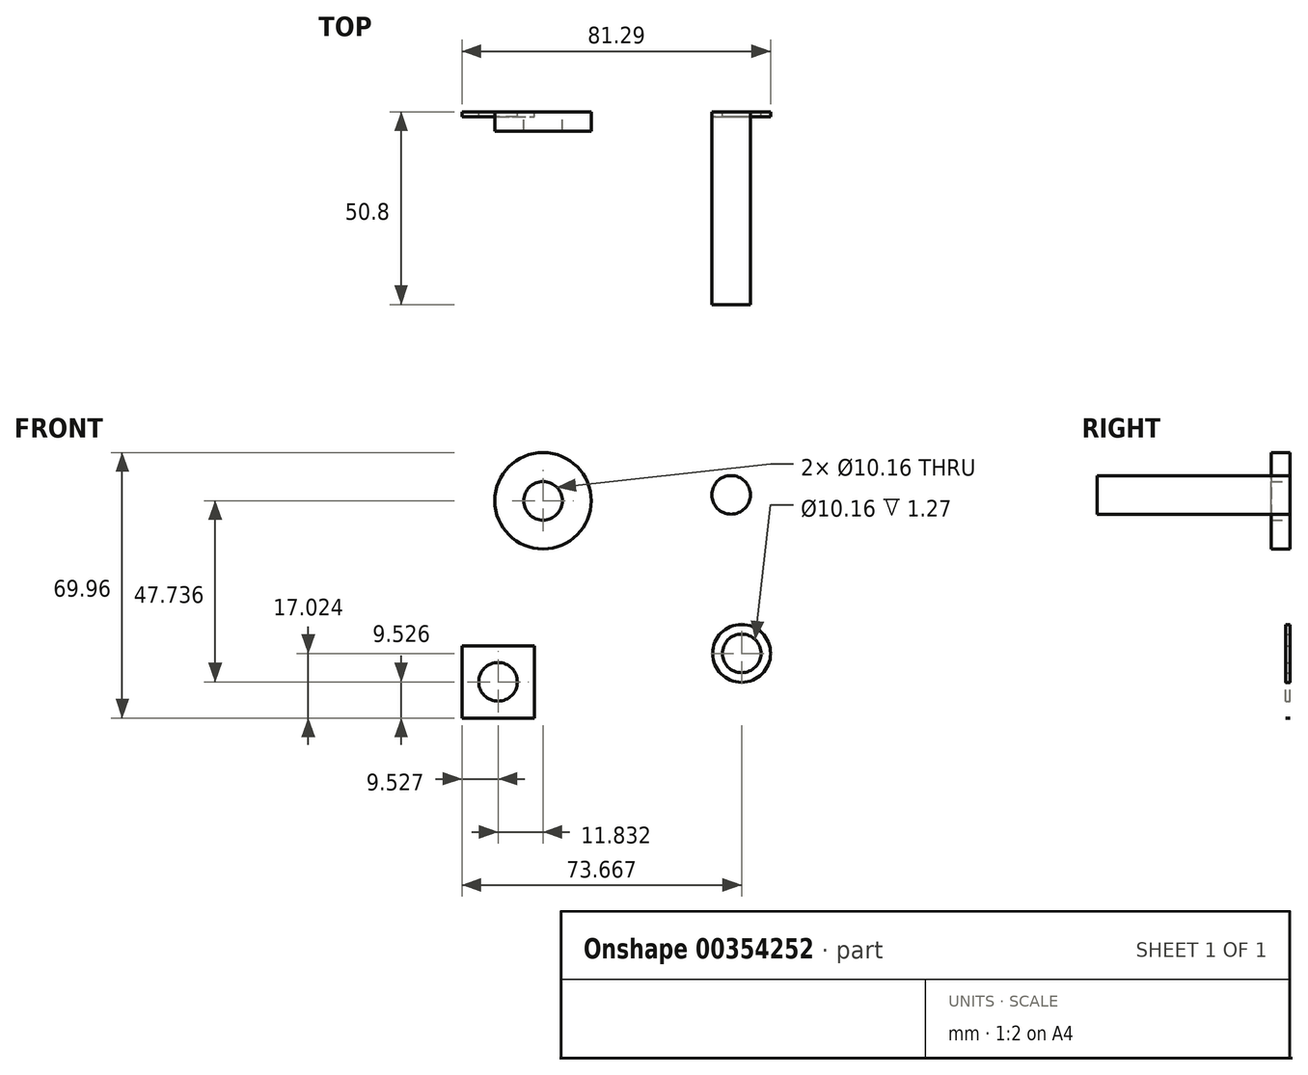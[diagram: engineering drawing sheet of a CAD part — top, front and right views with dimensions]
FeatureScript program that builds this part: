
annotation { "Feature Type Name" : "Feature", "Feature Type Description" : "" }
export const myFeature = defineFeature(function(context is Context, id is Id, definition is map)
    precondition{}
    {
        {
            var Q0;
            Q0=qCreatedBy(makeId("Front.planeOp"),FACE);
            var sketch = newSketch(context, id + "F0", { "sketchPlane" : qUnion([Q0])});
            skCircle(sketch, "E0", {"center": v(-24.76, 21.51) * mm, "radius": 12.7 * mm});
            skCircle(sketch, "E1", {"center": v(-24.76, 21.51) * mm, "radius": 5.08 * mm});
            skSolve(sketch);
        }
        {
            var Q0;
            Q0=makeQuery(id+"F0.imprint","IMPRINT",FACE,{"disambiguationData":[TD([[makeQuery(id+"F0.imprint","IMPRINT",EDGE,{"derivedFrom":sQuery(id+"F0.wireOp",EDGE,"E0")}),1.0]])]});
            extrude(context, id + "F1", {"entities" : qUnion([Q0]), "depth" : 5.08 * mm});
        }
        {
            var Q0;
            Q0=qCreatedBy(makeId("Front.planeOp"),FACE);
            var sketch = newSketch(context, id + "F2", { "sketchPlane" : qUnion([Q0])});
            skCircle(sketch, "E2", {"center": v(24.76, 23.06) * mm, "radius": 5.08 * mm});
            skSolve(sketch);
        }
        {
            var Q0;
            Q0=makeQuery(id+"F2.imprint","IMPRINT",FACE,{"disambiguationData":[TD([[makeQuery(id+"F2.imprint","IMPRINT",EDGE,{"derivedFrom":sQuery(id+"F2.wireOp",EDGE,"E2")}),1.0]])]});
            extrude(context, id + "F3", {"entities" : qUnion([Q0]), "depth" : 50.8 * mm});
        }
        {
            var Q0;
            Q0=qCreatedBy(makeId("Front.planeOp"),FACE);
            var sketch = newSketch(context, id + "F4", { "sketchPlane" : qUnion([Q0])});
            skCircle(sketch, "E3", {"center": v(-36.6, -26.22) * mm, "radius": 5.08 * mm});
            skLineSegment(sketch, "E4.bottom", {"start": v(-46.12, -16.7) * mm, "end": v(-27.07, -16.7) * mm});
            skLineSegment(sketch, "E4.top", {"start": v(-46.12, -35.75) * mm, "end": v(-27.07, -35.75) * mm});
            skLineSegment(sketch, "E4.left", {"start": v(-46.12, -16.7) * mm, "end": v(-46.12, -35.75) * mm});
            skLineSegment(sketch, "E4.right", {"start": v(-27.07, -16.7) * mm, "end": v(-27.07, -35.75) * mm});
            skSolve(sketch);
        }
        {
            var Q0;
            Q0=makeQuery(id+"F4.imprint","IMPRINT",FACE,{"disambiguationData":[TD([[makeQuery(id+"F4.imprint","IMPRINT",EDGE,{"derivedFrom":sQuery(id+"F4.wireOp",EDGE,"E3")}),-1.0]])]});
            extrude(context, id + "F5", {"entities" : qUnion([Q0]), "depth" : 1.27 * mm});
        }
        {
            var Q0;
            Q0=qCreatedBy(makeId("Front.planeOp"),FACE);
            var sketch = newSketch(context, id + "F6", { "sketchPlane" : qUnion([Q0])});
            skCircle(sketch, "E5", {"center": v(27.55, -18.73) * mm, "radius": 5.08 * mm});
            skCircle(sketch, "E6", {"center": v(27.55, -18.73) * mm, "radius": 7.62 * mm});
            skSolve(sketch);
        }
        {
            var Q0;
            Q0=makeQuery(id+"F6.imprint","IMPRINT",FACE,{"disambiguationData":[TD([[makeQuery(id+"F6.imprint","IMPRINT",EDGE,{"derivedFrom":sQuery(id+"F6.wireOp",EDGE,"E5")}),-1.0]])]});
            extrude(context, id + "F7", {"entities" : qUnion([Q0]), "depth" : 1.27 * mm});
        }
    });
